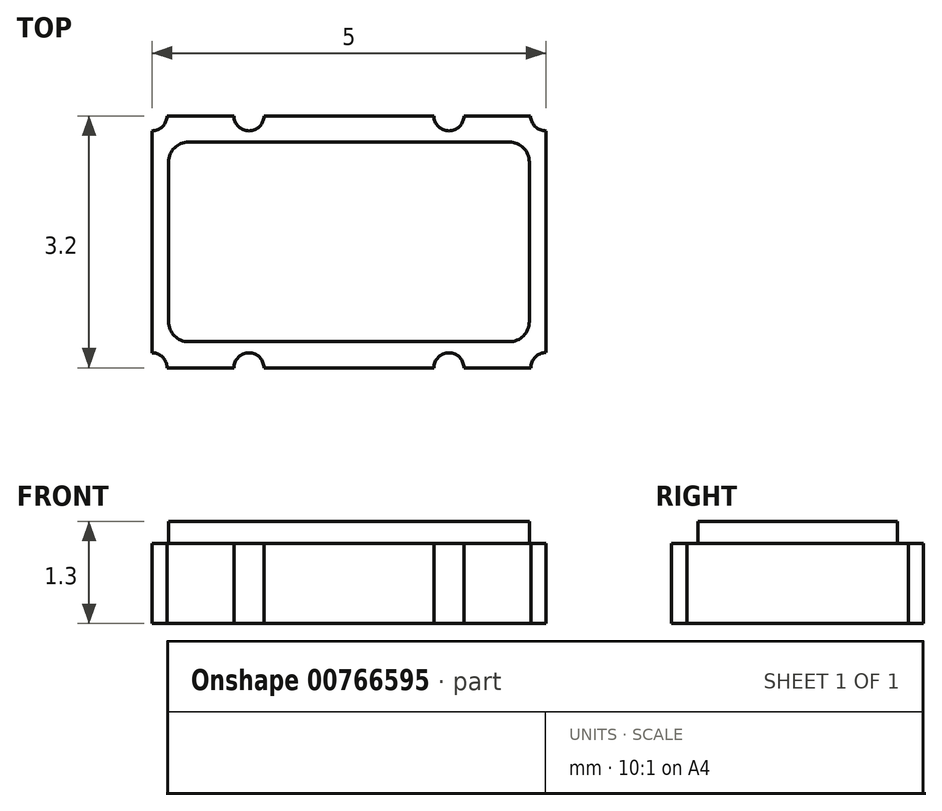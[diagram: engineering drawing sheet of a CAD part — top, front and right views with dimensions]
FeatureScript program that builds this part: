
annotation { "Feature Type Name" : "Feature", "Feature Type Description" : "" }
export const myFeature = defineFeature(function(context is Context, id is Id, definition is map)
    precondition{}
    {
        {
            var Q0;
            Q0=qCreatedBy(makeId("Top.planeOp"),FACE);
            var sketch = newSketch(context, id + "F0", { "sketchPlane" : qUnion([Q0])});
            skPoint(sketch, "E0.middle", {"position": v(0, 0) * mm});
            skLineSegment(sketch, "E1", {"start": v(-2.5, 1.4) * mm, "end": v(-2.5, -1.4) * mm});
            skLineSegment(sketch, "E2", {"start": v(-2.31, -1.6) * mm, "end": v(-1.46, -1.6) * mm});
            skLineSegment(sketch, "E3", {"start": v(-1.08, -1.6) * mm, "end": v(1.08, -1.6) * mm});
            skLineSegment(sketch, "E4", {"start": v(1.46, -1.6) * mm, "end": v(2.31, -1.6) * mm});
            skLineSegment(sketch, "E5", {"start": v(2.5, -1.4) * mm, "end": v(2.5, 1.4) * mm});
            skLineSegment(sketch, "E6", {"start": v(2.31, 1.6) * mm, "end": v(1.46, 1.6) * mm});
            skLineSegment(sketch, "E7", {"start": v(1.08, 1.6) * mm, "end": v(-1.08, 1.6) * mm});
            skLineSegment(sketch, "E8", {"start": v(-1.46, 1.6) * mm, "end": v(-2.31, 1.6) * mm});
            skArc(sketch, "E9", {"start": v(-2.31, 1.6) * mm, "mid": v(-2.37, 1.47) * mm, "end": v(-2.5, 1.4) * mm});
            skArc(sketch, "E10", {"start": v(-1.46, -1.6) * mm, "mid": v(-1.27, -1.4) * mm, "end": v(-1.08, -1.6) * mm});
            skArc(sketch, "E11", {"start": v(1.08, -1.6) * mm, "mid": v(1.27, -1.4) * mm, "end": v(1.46, -1.6) * mm});
            skArc(sketch, "E12", {"start": v(-2.5, -1.4) * mm, "mid": v(-2.37, -1.47) * mm, "end": v(-2.31, -1.6) * mm});
            skPoint(sketch, "E12.centerSnap0", {"position": v(0, -1.6) * mm});
            skArc(sketch, "E13", {"start": v(2.31, -1.6) * mm, "mid": v(2.37, -1.46) * mm, "end": v(2.5, -1.4) * mm});
            skArc(sketch, "E14", {"start": v(2.5, 1.4) * mm, "mid": v(2.37, 1.47) * mm, "end": v(2.3, 1.6) * mm});
            skArc(sketch, "E15", {"start": v(1.46, 1.6) * mm, "mid": v(1.27, 1.4) * mm, "end": v(1.08, 1.6) * mm});
            skArc(sketch, "E16", {"start": v(-1.08, 1.6) * mm, "mid": v(-1.27, 1.4) * mm, "end": v(-1.46, 1.6) * mm});
            skSolve(sketch);
        }
        {
            var Q0;
            Q0=makeQuery(id+"F0.imprint","IMPRINT",FACE,{"disambiguationData":[TD([[makeQuery(id+"F0.imprint","IMPRINT",EDGE,{"derivedFrom":sQuery(id+"F0.wireOp",EDGE,"E1")}),1.0]])]});
            extrude(context, id + "F1", {"entities" : qUnion([Q0]), "depth" : 1.02 * mm, "offsetDistance" : 25.4 * mm});
        }
        {
            var Q0;
            Q0=makeQuery(id+"F1.opExtrude","CAP_FACE",FACE,{"disambiguationData":[OSD([sQuery(id+"F0.wireOp",EDGE,"E1"),sQuery(id+"F0.wireOp",EDGE,"E2"),sQuery(id+"F0.wireOp",EDGE,"E3"),sQuery(id+"F0.wireOp",EDGE,"E4"),sQuery(id+"F0.wireOp",EDGE,"E5"),sQuery(id+"F0.wireOp",EDGE,"E6"),sQuery(id+"F0.wireOp",EDGE,"E7"),sQuery(id+"F0.wireOp",EDGE,"E8"),sQuery(id+"F0.wireOp",EDGE,"E9"),sQuery(id+"F0.wireOp",EDGE,"E10"),sQuery(id+"F0.wireOp",EDGE,"E11"),sQuery(id+"F0.wireOp",EDGE,"E12"),sQuery(id+"F0.wireOp",EDGE,"E13"),sQuery(id+"F0.wireOp",EDGE,"E14"),sQuery(id+"F0.wireOp",EDGE,"E15"),sQuery(id+"F0.wireOp",EDGE,"E16")])],"isStart":false});
            var sketch = newSketch(context, id + "F2", { "sketchPlane" : qUnion([Q0])});
            skLineSegment(sketch, "E17.bottom", {"start": v(-2.04, 1.27) * mm, "end": v(2.04, 1.27) * mm});
            skLineSegment(sketch, "E17.top", {"start": v(-2.04, -1.27) * mm, "end": v(2.04, -1.27) * mm});
            skLineSegment(sketch, "E17.left", {"start": v(-2.3, 1.01) * mm, "end": v(-2.3, -1.01) * mm});
            skLineSegment(sketch, "E17.right", {"start": v(2.3, 1.01) * mm, "end": v(2.3, -1.01) * mm});
            skPoint(sketch, "E17.middle", {"position": v(0, 0) * mm});
            skPoint(sketch, "E18.visualSharp", {"position": v(-2.3, 1.27) * mm});
            skArc(sketch, "E18.filletArc", {"start": v(-2.04, 1.27) * mm, "mid": v(-2.22, 1.2) * mm, "end": v(-2.3, 1.01) * mm});
            skPoint(sketch, "E19.visualSharp", {"position": v(-2.3, -1.27) * mm});
            skArc(sketch, "E19.filletArc", {"start": v(-2.3, -1.01) * mm, "mid": v(-2.22, -1.2) * mm, "end": v(-2.04, -1.27) * mm});
            skPoint(sketch, "E20.visualSharp", {"position": v(2.3, -1.27) * mm});
            skArc(sketch, "E20.filletArc", {"start": v(2.04, -1.27) * mm, "mid": v(2.22, -1.2) * mm, "end": v(2.3, -1.01) * mm});
            skPoint(sketch, "E21.visualSharp", {"position": v(2.3, 1.27) * mm});
            skArc(sketch, "E21.filletArc", {"start": v(2.3, 1.01) * mm, "mid": v(2.22, 1.2) * mm, "end": v(2.04, 1.27) * mm});
            skSolve(sketch);
        }
        {
            var Q0;
            Q0=makeQuery(id+"F2.imprint","IMPRINT",FACE,{"disambiguationData":[TD([[makeQuery(id+"F2.imprint","IMPRINT",EDGE,{"derivedFrom":sQuery(id+"F2.wireOp",EDGE,"E17.bottom")}),-1.0]])]});
            extrude(context, id + "F3", {"entities" : qUnion([Q0]), "operationType" : NewBodyOperationType.ADD, "depth" : 0.28 * mm, "offsetDistance" : 25.4 * mm});
        }
    });
